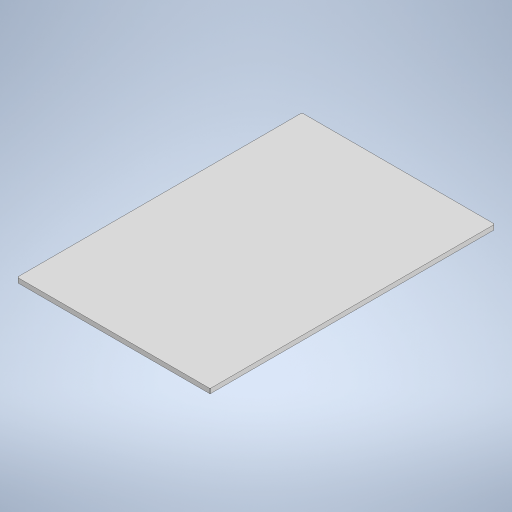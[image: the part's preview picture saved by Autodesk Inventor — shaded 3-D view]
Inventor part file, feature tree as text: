
AUTODESK INVENTOR PART (.ipt)
format: ipt  version: 2023.1 (Build 271208000, 208)  size: 235,520 bytes
history: native  units: in
note: dims shown in document units (in); Inventor stores cm internally (conversion verified against a paired STEP export)
features: extrude x3, sketch x3, chamfer x1
ambient origin geometry x8: Origin, YZ Plane, XZ Plane, XY Plane, X Axis, Y Axis, Z Axis, Center Point
bodies: Solid1 (feature_tree)
feature tree (7):
  extrude  "Extrusion1"  Depth=8.2677in
  chamfer  "Chamfer1"  Distance=0.1969in
  extrude  "Extrusion2"  Depth=11.811in
  extrude  "Extrusion3"  Depth=0.1969in
  sketch  "Sketch1"  dims[d0=12.2047in d1=8.2677in d2=0.1969in d3=0.0in]
  sketch  "Sketch2"  dims[d4=0.0394in d5=0.0787in d6=45.0deg d7=11.811in]
  sketch  "Sketch3"  dims[d8=7.874in d9=0.1969in d10=0.1969in d11=0.1969in d12=0.0in d13=11.0236in d14=7.0866in d15=0.3937in d16=0.3937in d17=0.1969in d18=0.0in]
